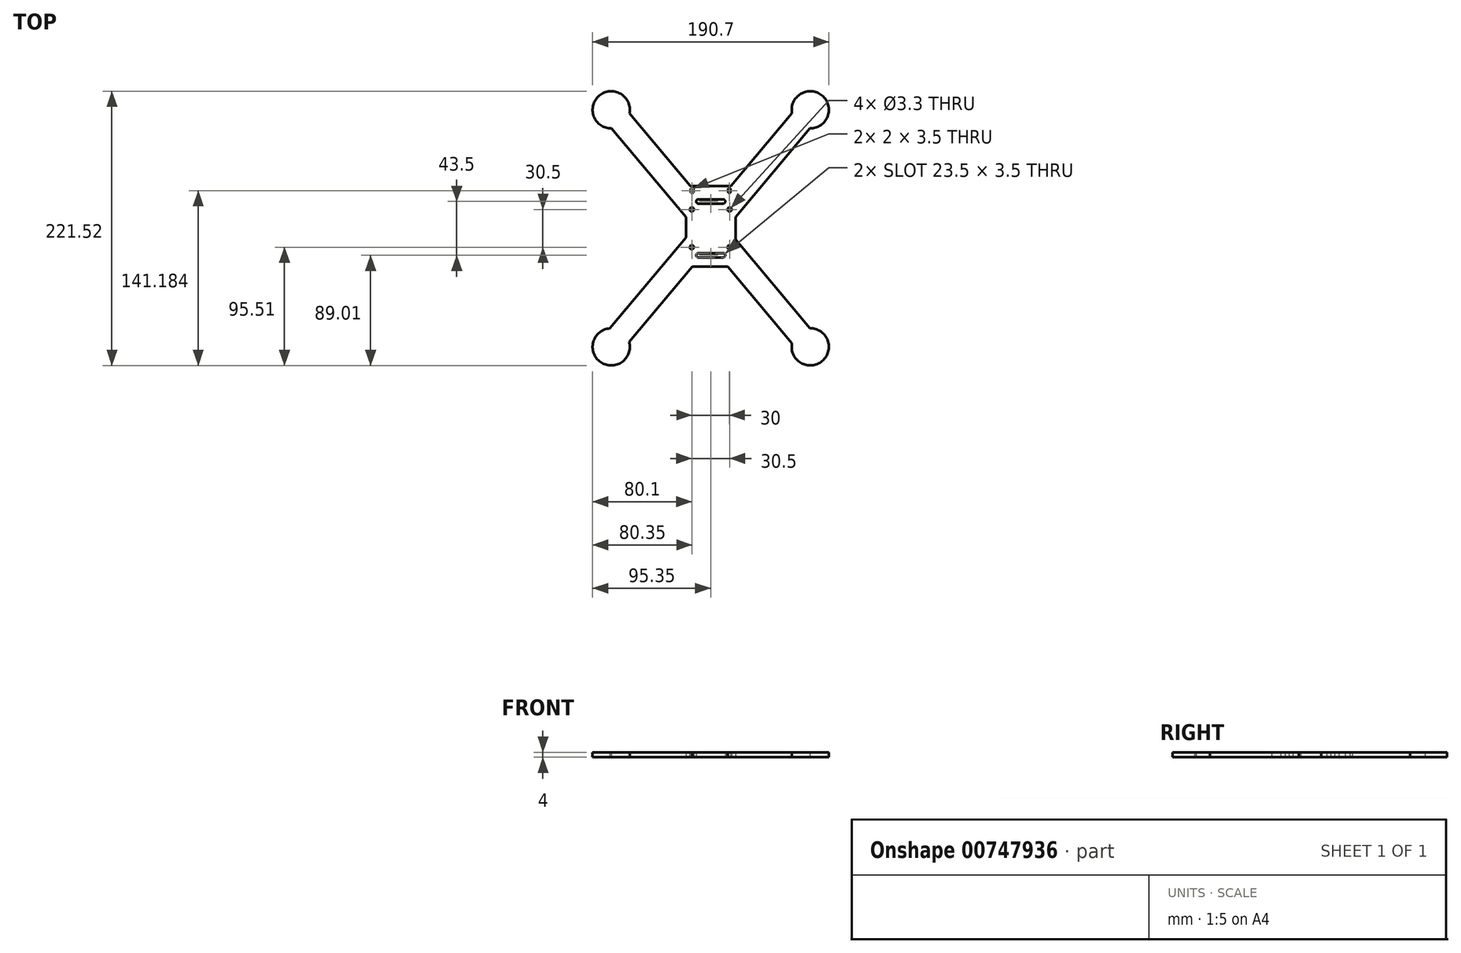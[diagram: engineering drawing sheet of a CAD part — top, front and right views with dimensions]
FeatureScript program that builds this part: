
annotation { "Feature Type Name" : "Feature", "Feature Type Description" : "" }
export const myFeature = defineFeature(function(context is Context, id is Id, definition is map)
    precondition{}
    {
        {
            var Q0;
            Q0=qCreatedBy(makeId("Top.planeOp"),FACE);
            var sketch = newSketch(context, id + "F0", { "sketchPlane" : qUnion([Q0])});
            skCircle(sketch, "E0", {"center": v(15.25, 15.25) * mm, "radius": 1.65 * mm});
            skCircle(sketch, "E1", {"center": v(15.25, -15.25) * mm, "radius": 1.65 * mm});
            skLineSegment(sketch, "E2", {"start": v(0, 0) * mm, "end": v(80.35, 95.76) * mm, "construction": true});
            skCircle(sketch, "E3", {"center": v(80.35, 95.76) * mm, "radius": 67.5 * mm, "construction": true});
            skLineSegment(sketch, "E4", {"start": v(0, 0) * mm, "end": v(80.35, -95.76) * mm, "construction": true});
            skCircle(sketch, "E5", {"center": v(80.35, -95.76) * mm, "radius": 67.5 * mm, "construction": true});
            skCircle(sketch, "E6", {"center": v(-15.25, 15.25) * mm, "radius": 1.65 * mm});
            skCircle(sketch, "E7", {"center": v(-15.25, -15.25) * mm, "radius": 1.65 * mm});
            skLineSegment(sketch, "E8.left", {"start": v(-20, 20) * mm, "end": v(-20, -20) * mm});
            skLineSegment(sketch, "E8.right", {"start": v(20, 20) * mm, "end": v(20, -20) * mm});
            skPoint(sketch, "E8.middle", {"position": v(0, 0) * mm});
            skLineSegment(sketch, "E9", {"start": v(80.35, 95.76) * mm, "end": v(73.07, 101.86) * mm});
            skLineSegment(sketch, "E10", {"start": v(73.07, 101.86) * mm, "end": v(87.63, 89.65) * mm});
            skLineSegment(sketch, "E11", {"start": v(20, 9.06) * mm, "end": v(87.63, 89.65) * mm});
            skLineSegment(sketch, "E12", {"start": v(73.07, 101.86) * mm, "end": v(5.95, 21.87) * mm});
            skLineSegment(sketch, "E13", {"start": v(80.35, -95.76) * mm, "end": v(87.63, -89.65) * mm});
            skLineSegment(sketch, "E14", {"start": v(87.63, -89.65) * mm, "end": v(73.07, -101.86) * mm});
            skLineSegment(sketch, "E15", {"start": v(73.07, -101.86) * mm, "end": v(4.38, -20) * mm});
            skLineSegment(sketch, "E16", {"start": v(87.63, -89.65) * mm, "end": v(20, -9.06) * mm});
            skCircle(sketch, "E17", {"center": v(80.35, -95.76) * mm, "radius": 15 * mm});
            skCircle(sketch, "E18", {"center": v(80.35, 95.76) * mm, "radius": 15 * mm});
            skLineSegment(sketch, "E19", {"start": v(0, 0) * mm, "end": v(-80.35, 95.76) * mm, "construction": true});
            skLineSegment(sketch, "E20", {"start": v(0, 0) * mm, "end": v(-80.35, -95.76) * mm, "construction": true});
            skLineSegment(sketch, "E21", {"start": v(-80.35, 95.76) * mm, "end": v(-73.07, 101.86) * mm});
            skLineSegment(sketch, "E22", {"start": v(-73.07, 101.86) * mm, "end": v(-87.63, 89.65) * mm});
            skLineSegment(sketch, "E23", {"start": v(-87.63, 89.65) * mm, "end": v(-20, 9.06) * mm});
            skLineSegment(sketch, "E24", {"start": v(-73.07, 101.86) * mm, "end": v(-4.38, 20) * mm});
            skCircle(sketch, "E25", {"center": v(-80.35, 95.76) * mm, "radius": 15 * mm});
            skLineSegment(sketch, "E26", {"start": v(-80.35, -95.76) * mm, "end": v(-73.84, -101.22) * mm});
            skLineSegment(sketch, "E27", {"start": v(-73.84, -101.22) * mm, "end": v(-88.4, -89) * mm});
            skLineSegment(sketch, "E28", {"start": v(-73.84, -101.22) * mm, "end": v(-5.69, -20) * mm});
            skLineSegment(sketch, "E29", {"start": v(-88.4, -89) * mm, "end": v(-20, -7.5) * mm});
            skCircle(sketch, "E30", {"center": v(-80.35, -95.76) * mm, "radius": 15 * mm});
            skLineSegment(sketch, "E31.top", {"start": v(-20, -31) * mm, "end": v(20, -31) * mm});
            skLineSegment(sketch, "E31.left", {"start": v(-20, -20) * mm, "end": v(-20, -31) * mm});
            skLineSegment(sketch, "E31.right", {"start": v(20, -20) * mm, "end": v(20, -31) * mm});
            skLineSegment(sketch, "E32.top", {"start": v(-20, 34.17) * mm, "end": v(20, 34.17) * mm});
            skLineSegment(sketch, "E32.left", {"start": v(-20, 20) * mm, "end": v(-20, 34.17) * mm});
            skLineSegment(sketch, "E32.right", {"start": v(20, 20) * mm, "end": v(20, 34.17) * mm});
            skLineSegment(sketch, "E33", {"start": v(0, 20) * mm, "end": v(0, 21.75) * mm, "construction": true});
            skLineSegment(sketch, "E34.bottom", {"start": v(10, 20) * mm, "end": v(-4.38, 20) * mm});
            skLineSegment(sketch, "E34.top", {"start": v(10, 23.5) * mm, "end": v(-10, 23.5) * mm});
            skLineSegment(sketch, "E34.left", {"start": v(10, 20) * mm, "end": v(10, 23.5) * mm});
            skLineSegment(sketch, "E34.right", {"start": v(-10, 20) * mm, "end": v(-10, 23.5) * mm});
            skPoint(sketch, "E34.middle", {"position": v(0, 21.75) * mm});
            skCircle(sketch, "E35", {"center": v(-10, 21.75) * mm, "radius": 1.75 * mm});
            skCircle(sketch, "E36", {"center": v(10, 21.75) * mm, "radius": 1.75 * mm});
            skLineSegment(sketch, "E37", {"start": v(0, -20) * mm, "end": v(0, -21.75) * mm, "construction": true});
            skLineSegment(sketch, "E38.bottom", {"start": v(10, -20) * mm, "end": v(-10, -20) * mm});
            skLineSegment(sketch, "E38.top", {"start": v(10, -23.5) * mm, "end": v(-10, -23.5) * mm});
            skLineSegment(sketch, "E38.left", {"start": v(10, -20) * mm, "end": v(10, -23.5) * mm});
            skLineSegment(sketch, "E38.right", {"start": v(-10, -20) * mm, "end": v(-10, -23.5) * mm});
            skPoint(sketch, "E38.middle", {"position": v(0, -21.75) * mm});
            skCircle(sketch, "E39", {"center": v(10, -21.75) * mm, "radius": 1.75 * mm});
            skCircle(sketch, "E40", {"center": v(-10, -21.75) * mm, "radius": 1.75 * mm});
            skLineSegment(sketch, "E41.trimOffspring", {"start": v(-10, -20) * mm, "end": v(10, -20) * mm});
            skLineSegment(sketch, "E42.trimOffspring", {"start": v(-10, 20) * mm, "end": v(10, 20) * mm});
            skLineSegment(sketch, "E43.trimOffspring", {"start": v(0, 20) * mm, "end": v(10, 20) * mm});
            skLineSegment(sketch, "E44", {"start": v(0, 34.17) * mm, "end": v(-14, 34.17) * mm, "construction": true});
            skLineSegment(sketch, "E45", {"start": v(0, 34.17) * mm, "end": v(14, 34.17) * mm, "construction": true});
            skLineSegment(sketch, "E46", {"start": v(-14, 34.17) * mm, "end": v(-14, 32.17) * mm, "construction": true});
            skLineSegment(sketch, "E47.bottom", {"start": v(-14, 32.17) * mm, "end": v(-16, 32.17) * mm});
            skLineSegment(sketch, "E47.top", {"start": v(-14, 28.67) * mm, "end": v(-16, 28.67) * mm});
            skLineSegment(sketch, "E47.left", {"start": v(-14, 32.17) * mm, "end": v(-14, 28.67) * mm});
            skLineSegment(sketch, "E47.right", {"start": v(-16, 32.17) * mm, "end": v(-16, 28.67) * mm});
            skLineSegment(sketch, "E48.MirrorCS", {"start": v(16, 32.17) * mm, "end": v(16, 28.67) * mm});
            skLineSegment(sketch, "E49.MirrorCS", {"start": v(14, 32.17) * mm, "end": v(16, 32.17) * mm});
            skLineSegment(sketch, "E50.MirrorCS", {"start": v(14, 32.17) * mm, "end": v(14, 28.67) * mm});
            skLineSegment(sketch, "E51.MirrorCS", {"start": v(14, 28.67) * mm, "end": v(16, 28.67) * mm});
            skLineSegment(sketch, "E52", {"start": v(16, 32.17) * mm, "end": v(16, 33.85) * mm, "construction": true});
            skLineSegment(sketch, "E53", {"start": v(-16, 32.17) * mm, "end": v(-16, 33.85) * mm, "construction": true});
            skSolve(sketch);
        }
        {
            var Q0;
            Q0=makeQuery(id+"F0.imprint","IMPRINT",FACE,{"disambiguationData":[TD([[makeQuery(id+"F0.imprint","IMPRINT",EDGE,{"derivedFrom":sQuery(id+"F0.wireOp",EDGE,"E0")}),-1.0]])]});
            var Q1;
            {var subQ5=sQuery(id+"F0.wireOp",EDGE,"E32.left");Q1=makeQuery(id+"F0.imprint","IMPRINT",FACE,{"disambiguationData":[TD([[makeQuery(id+"F0.imprint","IMPRINT",EDGE,{"derivedFrom":subQ5}),1.0]])]});}
            var Q2;
            {var subQ5=sQuery(id+"F0.wireOp",EDGE,"E32.top");var subQ6=sQuery(id+"F0.wireOp",EDGE,"E12");var subQ7=makeQuery(id+"F0.imprint","INTERSECT",VERTEX,{"derivedFrom":[subQ6,subQ5]});Q2=makeQuery(id+"F0.imprint","IMPRINT",FACE,{"disambiguationData":[TD([[makeQuery(id+"F0.imprint","IMPRINT",EDGE,{"disambiguationData":[TD([[subQ7,-1.0]])],"derivedFrom":subQ6}),-1.0]])]});}
            var Q3;
            {var subQ0=sQuery(id+"F0.wireOp",EDGE,"E32.right");Q3=makeQuery(id+"F0.imprint","IMPRINT",FACE,{"disambiguationData":[TD([[makeQuery(id+"F0.imprint","IMPRINT",EDGE,{"derivedFrom":subQ0}),1.0]])]});}
            var Q4;
            {var subQ0=sQuery(id+"F0.wireOp",EDGE,"E32.left");Q4=makeQuery(id+"F0.imprint","IMPRINT",FACE,{"disambiguationData":[TD([[makeQuery(id+"F0.imprint","IMPRINT",EDGE,{"derivedFrom":subQ0}),-1.0]])]});}
            var Q5;
            {var subQ5=sQuery(id+"F0.wireOp",EDGE,"E32.right");Q5=makeQuery(id+"F0.imprint","IMPRINT",FACE,{"disambiguationData":[TD([[makeQuery(id+"F0.imprint","IMPRINT",EDGE,{"derivedFrom":subQ5}),-1.0]])]});}
            var Q6;
            {var subQ9=sQuery(id+"F0.wireOp",EDGE,"E31.right");Q6=makeQuery(id+"F0.imprint","IMPRINT",FACE,{"disambiguationData":[TD([[makeQuery(id+"F0.imprint","IMPRINT",EDGE,{"derivedFrom":subQ9}),1.0]])]});}
            var Q7;
            {var subQ0=sQuery(id+"F0.wireOp",EDGE,"E31.top");var subQ1=sQuery(id+"F0.wireOp",EDGE,"E15");var subQ2=makeQuery(id+"F0.imprint","INTERSECT",VERTEX,{"derivedFrom":[subQ1,subQ0]});Q7=makeQuery(id+"F0.imprint","IMPRINT",FACE,{"disambiguationData":[TD([[makeQuery(id+"F0.imprint","IMPRINT",EDGE,{"disambiguationData":[TD([[subQ2,-1.0]])],"derivedFrom":subQ1}),1.0]])]});}
            var Q8;
            {var subQ7=sQuery(id+"F0.wireOp",EDGE,"E31.left");Q8=makeQuery(id+"F0.imprint","IMPRINT",FACE,{"disambiguationData":[TD([[makeQuery(id+"F0.imprint","IMPRINT",EDGE,{"derivedFrom":subQ7}),-1.0]])]});}
            var Q9;
            {var subQ1=sQuery(id+"F0.wireOp",EDGE,"E22");var subQ8=makeQuery(id+"F0.imprint","IMPRINT",VERTEX,{"derivedFrom":subQ1});Q9=makeQuery(id+"F0.imprint","IMPRINT",FACE,{"disambiguationData":[TD([[makeQuery(id+"F0.imprint","IMPRINT",EDGE,{"disambiguationData":[TD([[subQ8,1.0]])],"derivedFrom":subQ1}),1.0]])]});}
            var Q10;
            {var subQ1=sQuery(id+"F0.wireOp",EDGE,"E22");var subQ8=makeQuery(id+"F0.imprint","IMPRINT",VERTEX,{"derivedFrom":subQ1});Q10=makeQuery(id+"F0.imprint","IMPRINT",FACE,{"disambiguationData":[TD([[makeQuery(id+"F0.imprint","IMPRINT",EDGE,{"disambiguationData":[TD([[subQ8,1.0]])],"derivedFrom":subQ1}),-1.0]])]});}
            var Q11;
            {var subQ1=sQuery(id+"F0.wireOp",EDGE,"E10");var subQ8=makeQuery(id+"F0.imprint","IMPRINT",VERTEX,{"derivedFrom":subQ1});Q11=makeQuery(id+"F0.imprint","IMPRINT",FACE,{"disambiguationData":[TD([[makeQuery(id+"F0.imprint","IMPRINT",EDGE,{"disambiguationData":[TD([[subQ8,1.0]])],"derivedFrom":subQ1}),-1.0]])]});}
            var Q12;
            {var subQ1=sQuery(id+"F0.wireOp",EDGE,"E10");var subQ8=makeQuery(id+"F0.imprint","IMPRINT",VERTEX,{"derivedFrom":subQ1});Q12=makeQuery(id+"F0.imprint","IMPRINT",FACE,{"disambiguationData":[TD([[makeQuery(id+"F0.imprint","IMPRINT",EDGE,{"disambiguationData":[TD([[subQ8,1.0]])],"derivedFrom":subQ1}),1.0]])]});}
            var Q13;
            {var subQ1=sQuery(id+"F0.wireOp",EDGE,"E14");var subQ8=makeQuery(id+"F0.imprint","IMPRINT",VERTEX,{"derivedFrom":subQ1});Q13=makeQuery(id+"F0.imprint","IMPRINT",FACE,{"disambiguationData":[TD([[makeQuery(id+"F0.imprint","IMPRINT",EDGE,{"disambiguationData":[TD([[subQ8,1.0]])],"derivedFrom":subQ1}),1.0]])]});}
            var Q14;
            {var subQ1=sQuery(id+"F0.wireOp",EDGE,"E14");var subQ8=makeQuery(id+"F0.imprint","IMPRINT",VERTEX,{"derivedFrom":subQ1});Q14=makeQuery(id+"F0.imprint","IMPRINT",FACE,{"disambiguationData":[TD([[makeQuery(id+"F0.imprint","IMPRINT",EDGE,{"disambiguationData":[TD([[subQ8,1.0]])],"derivedFrom":subQ1}),-1.0]])]});}
            var Q15;
            {var subQ1=sQuery(id+"F0.wireOp",EDGE,"E27");var subQ8=makeQuery(id+"F0.imprint","IMPRINT",VERTEX,{"derivedFrom":subQ1});Q15=makeQuery(id+"F0.imprint","IMPRINT",FACE,{"disambiguationData":[TD([[makeQuery(id+"F0.imprint","IMPRINT",EDGE,{"disambiguationData":[TD([[subQ8,1.0]])],"derivedFrom":subQ1}),-1.0]])]});}
            var Q16;
            {var subQ1=sQuery(id+"F0.wireOp",EDGE,"E27");var subQ8=makeQuery(id+"F0.imprint","IMPRINT",VERTEX,{"derivedFrom":subQ1});Q16=makeQuery(id+"F0.imprint","IMPRINT",FACE,{"disambiguationData":[TD([[makeQuery(id+"F0.imprint","IMPRINT",EDGE,{"disambiguationData":[TD([[subQ8,1.0]])],"derivedFrom":subQ1}),1.0]])]});}
            extrude(context, id + "F1", {"entities" : qUnion([Q0, Q1, Q2, Q3, Q4, Q5, Q6, Q7, Q8, Q9, Q10, Q11, Q12, Q13, Q14, Q15, Q16]), "depth" : 4 * mm, "offsetDistance" : 25 * mm});
        }
    });
